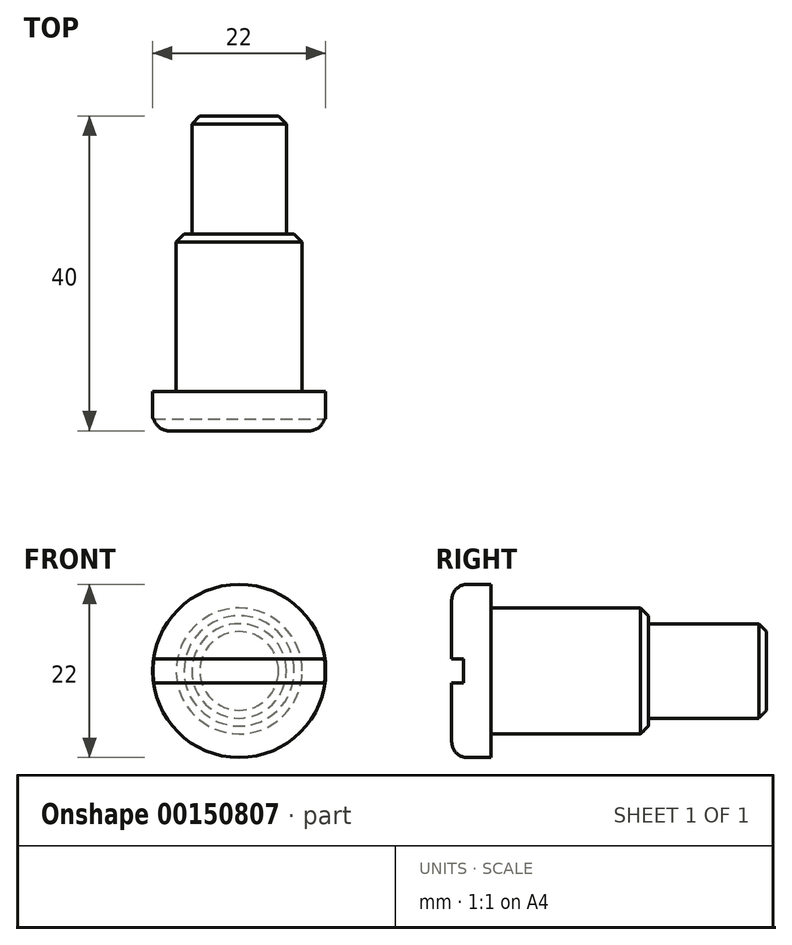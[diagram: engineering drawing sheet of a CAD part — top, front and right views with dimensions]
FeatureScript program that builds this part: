
annotation { "Feature Type Name" : "Feature", "Feature Type Description" : "" }
export const myFeature = defineFeature(function(context is Context, id is Id, definition is map)
    precondition{}
    {
        {
            var Q0;
            Q0=qCreatedBy(makeId("Front.planeOp"),FACE);
            var sketch = newSketch(context, id + "F0", { "sketchPlane" : qUnion([Q0])});
            skCircle(sketch, "E0", {"center": v(0, 0) * mm, "radius": 11 * mm});
            skSolve(sketch);
        }
        {
            var Q0;
            Q0=qSketchRegion(id+"F0",true);
            extrude(context, id + "F1", {"entities" : qUnion([Q0]), "depth" : 5 * mm});
        }
        {
            var Q0;
            Q0=makeQuery(id+"F1.opExtrude","CAP_EDGE",EDGE,{"disambiguationData":[OSD([sQuery(id+"F0.wireOp",EDGE,"E0")])],"isStart":false});
            fillet(context, id + "F2", {"entities" : qUnion([Q0]), "radius" : 2 * mm, "tangentPropagation" : true, "allowEdgeOverflow" : false});
        }
        {
            var Q0;
            Q0=qCreatedBy(makeId("Front.planeOp"),FACE);
            var sketch = newSketch(context, id + "F3", { "sketchPlane" : qUnion([Q0])});
            skCircle(sketch, "E1", {"center": v(0, 0) * mm, "radius": 8 * mm});
            skCircle(sketch, "E2", {"center": v(0, 0) * mm, "radius": 6 * mm});
            skSolve(sketch);
        }
        {
            var Q0;
            Q0=qSketchRegion(id+"F3",true);
            extrude(context, id + "F4", {"entities" : qUnion([Q0]), "operationType" : NewBodyOperationType.ADD, "oppositeDirection" : true, "depth" : 20 * mm});
        }
        {
            var Q0;
            Q0=makeQuery(id+"F4.boolean.opBoolean","SPLIT",FACE,{"disambiguationData":[TD([makeQuery(id+"F4.opExtrude","SWEPT_FACE",FACE,{"disambiguationData":[OSD([sQuery(id+"F3.wireOp",EDGE,"E2")])]})])],"derivedFrom":makeQuery(id+"F1.opExtrude","CAP_FACE",FACE,{"disambiguationData":[OSD([sQuery(id+"F0.wireOp",EDGE,"E0")])],"isStart":true})});
            extrude(context, id + "F5", {"entities" : qUnion([Q0]), "operationType" : NewBodyOperationType.ADD, "depth" : 35 * mm});
        }
        {
            var Q0;
            Q0=makeQuery(id+"F5.opExtrude","CAP_EDGE",EDGE,{"disambiguationData":[OSD([sQuery(id+"F3.wireOp",EDGE,"E2")])],"isStart":false});
            var Q1;
            Q1=makeQuery(id+"F4.opExtrude","CAP_EDGE",EDGE,{"disambiguationData":[OSD([sQuery(id+"F3.wireOp",EDGE,"E1")])],"isStart":false});
            chamfer(context, id + "F6", {"entities" : qUnion([Q0, Q1]), "chamferType" : ChamferType.OFFSET_ANGLE, "width" : 1 * mm, "oppositeDirection" : false, "angle" : 45 * degree, "tangentPropagation" : true});
        }
        {
            var Q0;
            Q0=qCreatedBy(makeId("Right.planeOp"),FACE);
            var sketch = newSketch(context, id + "F7", { "sketchPlane" : qUnion([Q0])});
            skLineSegment(sketch, "E3.0", {"start": v(-5, -9) * mm, "end": v(-5, -1.5) * mm, "construction": true});
            skLineSegment(sketch, "E4.0", {"start": v(-3, 11) * mm, "end": v(-3, -11) * mm, "construction": true});
            skArc(sketch, "E5", {"start": v(-5, -9) * mm, "mid": v(-4.41, -10.41) * mm, "end": v(-3, -11) * mm, "construction": true});
            skArc(sketch, "E6", {"start": v(-3, 11) * mm, "mid": v(-4.41, 10.41) * mm, "end": v(-5, 9) * mm, "construction": true});
            skLineSegment(sketch, "E7", {"start": v(-3, 11) * mm, "end": v(0, 11) * mm, "construction": true});
            skLineSegment(sketch, "E8", {"start": v(0, -11) * mm, "end": v(-3, -11) * mm, "construction": true});
            skLineSegment(sketch, "E9", {"start": v(-5, 1.5) * mm, "end": v(-3.5, 1.5) * mm});
            skLineSegment(sketch, "E10", {"start": v(-3.5, 1.5) * mm, "end": v(-3.5, -1.5) * mm});
            skLineSegment(sketch, "E11", {"start": v(-3.5, -1.5) * mm, "end": v(-5, -1.5) * mm});
            skLineSegment(sketch, "E12.trimOffspring", {"start": v(-5, 1.5) * mm, "end": v(-5, 9) * mm, "construction": true});
            skLineSegment(sketch, "E13", {"start": v(-5, 1.5) * mm, "end": v(-5, -1.5) * mm});
            skSolve(sketch);
        }
        {
            var Q0;
            Q0=makeQuery(id+"F7.imprint","IMPRINT",FACE,{"disambiguationData":[TD([[makeQuery(id+"F7.imprint","IMPRINT",EDGE,{"derivedFrom":sQuery(id+"F7.wireOp",EDGE,"E9")}),-1.0]])]});
            extrude(context, id + "F8", {"entities" : qUnion([Q0]), "operationType" : NewBodyOperationType.REMOVE, "oppositeDirection" : true, "depth" : 25 * mm, "symmetric" : true});
        }
    });
